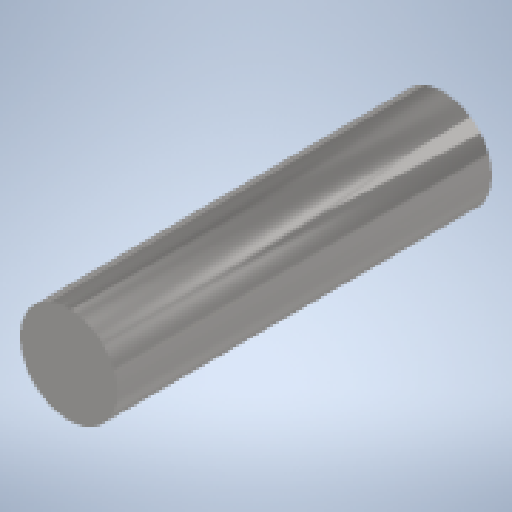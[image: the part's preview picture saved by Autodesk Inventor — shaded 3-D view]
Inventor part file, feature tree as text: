
AUTODESK INVENTOR PART (.ipt)
format: ipt  version: 2023 (Build 270158000, 158)  size: 249,856 bytes
history: native  units: mm
features: extrude x1, sketch x1
ambient origin geometry x8: Origin, YZ Plane, XZ Plane, XY Plane, X Axis, Y Axis, Z Axis, Center Point
bodies: Solid1 (feature_tree)
feature tree (2):
  extrude  "Extrusion1"  Depth=54.0mm TaperAngle=0.0deg
  sketch  "Sketch1"  dims[d0=14.0mm d1=54.0mm d2=0.0mm]
